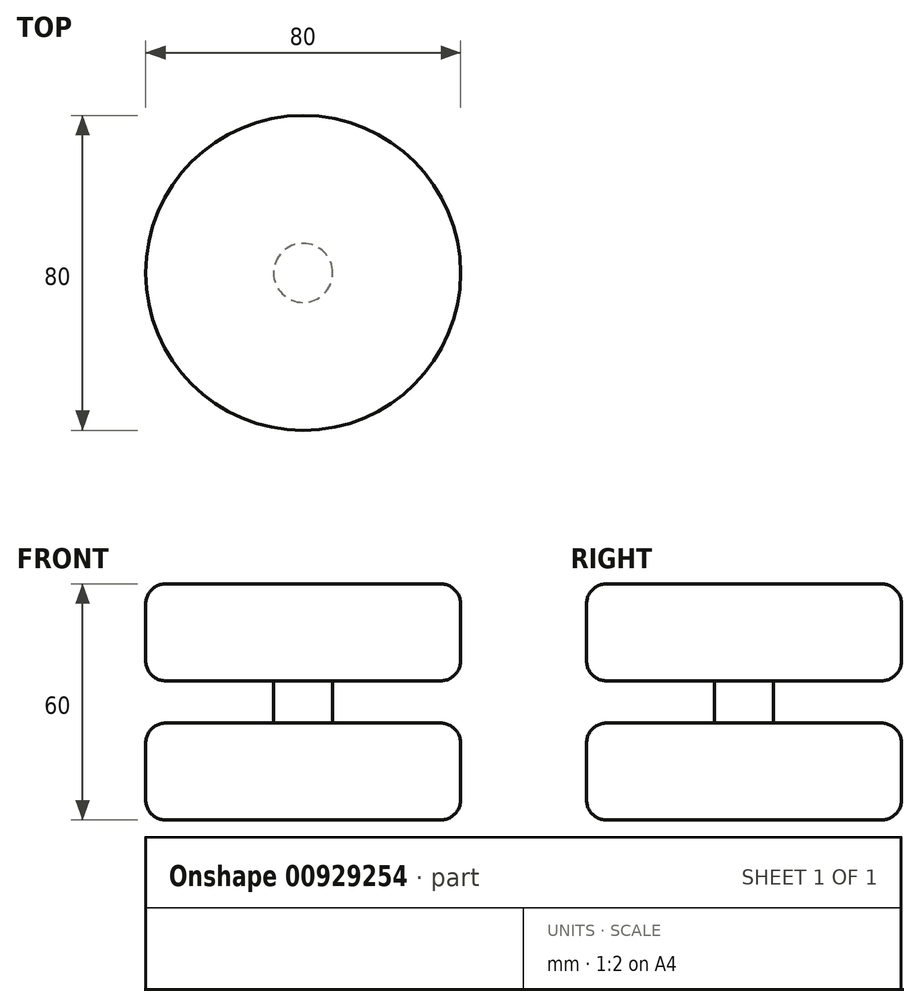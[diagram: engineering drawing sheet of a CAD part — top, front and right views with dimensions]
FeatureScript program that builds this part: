
annotation { "Feature Type Name" : "Feature", "Feature Type Description" : "" }
export const myFeature = defineFeature(function(context is Context, id is Id, definition is map)
    precondition{}
    {
        {
            var Q0;
            Q0=qCreatedBy(makeId("Top.planeOp"),FACE);
            var sketch = newSketch(context, id + "F0", { "sketchPlane" : qUnion([Q0])});
            skCircle(sketch, "E0", {"center": v(0, 0) * mm, "radius": 40 * mm});
            skSolve(sketch);
        }
        {
            var Q0;
            Q0 = qSketchRegion(id + "F0", true);
            extrude(context, id + "F1", {"entities" : qUnion([Q0]), "depth" : 24.64 * mm, "offsetDistance" : 25.4 * mm});
        }
        {
            var Q0;
            Q0=makeQuery(id+"F1.opExtrude","CAP_EDGE",EDGE,{"disambiguationData":[OSD([sQuery(id+"F0.wireOp",EDGE,"E0")])],"isStart":false});
            var Q1;
            Q1=makeQuery(id+"F1.opExtrude","CAP_EDGE",EDGE,{"disambiguationData":[OSD([sQuery(id+"F0.wireOp",EDGE,"E0")])],"isStart":true});
            fillet(context, id + "F2", {"entities" : qUnion([Q0, Q1]), "radius" : 5.08 * mm, "tangentPropagation" : true, "allowEdgeOverflow" : false});
        }
        {
            var Q0;
            Q0=qCreatedBy(makeId("Top.planeOp"),FACE);
            var sketch = newSketch(context, id + "F3", { "sketchPlane" : qUnion([Q0])});
            skCircle(sketch, "E1", {"center": v(0, 0) * mm, "radius": 7.5 * mm});
            skSolve(sketch);
        }
        {
            var Q0;
            Q0=makeQuery(id+"F3.imprint","IMPRINT",FACE,{"disambiguationData":[TD([[makeQuery(id+"F3.imprint","IMPRINT",EDGE,{"derivedFrom":sQuery(id+"F3.wireOp",EDGE,"E1")}),1.0]])]});
            extrude(context, id + "F4", {"entities" : qUnion([Q0]), "operationType" : NewBodyOperationType.ADD, "depth" : 30 * mm, "offsetDistance" : 25 * mm});
        }
        {
            var Q0;
            Q0=makeQuery(id+"F1.opExtrude","SWEPT_BODY",BODY,{"disambiguationData":[OSD([sQuery(id+"F0.wireOp",EDGE,"E0")])]});
            var Q1;
            Q1=makeQuery(id+"F4.opExtrude","CAP_FACE",FACE,{"disambiguationData":[OSD([sQuery(id+"F3.wireOp",EDGE,"E1")])],"isStart":false});
            mirror(context, id + "F5", {"operationType" : NewBodyOperationType.ADD, "entities" : qUnion([Q0]), "mirrorPlane" : qUnion([Q1])});
        }
    });
